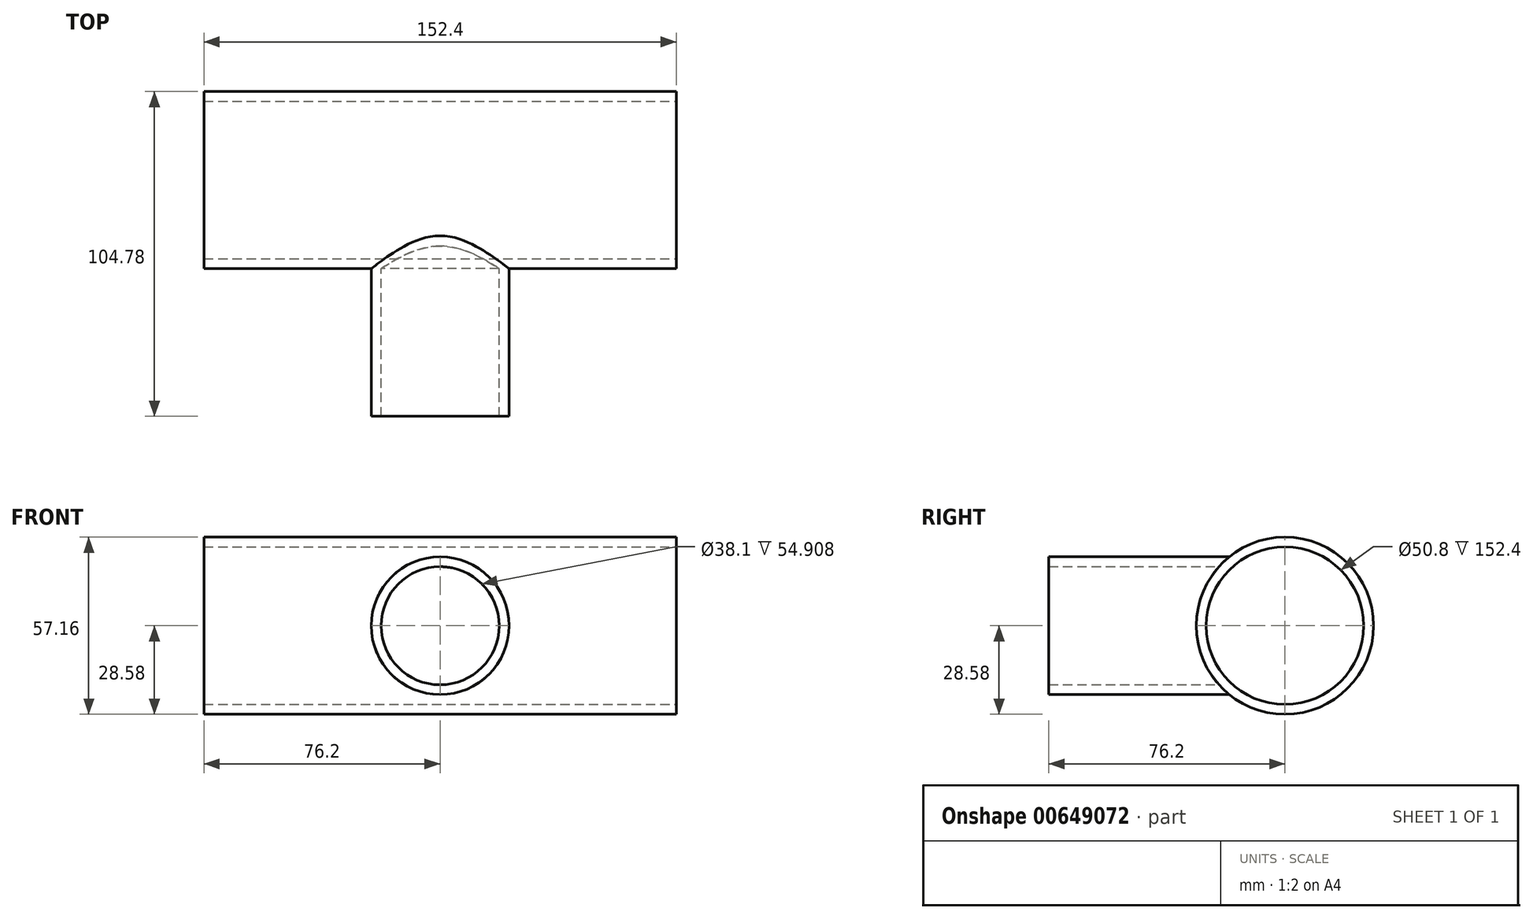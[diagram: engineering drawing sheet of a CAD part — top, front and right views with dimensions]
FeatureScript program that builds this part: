
annotation { "Feature Type Name" : "Feature", "Feature Type Description" : "" }
export const myFeature = defineFeature(function(context is Context, id is Id, definition is map)
    precondition{}
    {
        {
            var Q0;
            Q0=qCreatedBy(makeId("Right.planeOp"),FACE);
            var sketch = newSketch(context, id + "F0", { "sketchPlane" : qUnion([Q0])});
            skCircle(sketch, "E0", {"center": v(0, 0) * mm, "radius": 28.58 * mm});
            skSolve(sketch);
        }
        {
            var Q0;
            Q0 = qSketchRegion(id + "F0", true);
            extrude(context, id + "F1", {"entities" : qUnion([Q0]), "depth" : 76.2 * mm, "offsetDistance" : 25.4 * mm, "hasSecondDirection" : true, "secondDirectionOppositeDirection" : true, "secondDirectionDepth" : 76.2 * mm});
        }
        {
            var Q0;
            Q0=qCreatedBy(makeId("Front.planeOp"),FACE);
            var sketch = newSketch(context, id + "F2", { "sketchPlane" : qUnion([Q0])});
            skCircle(sketch, "E1", {"center": v(0, 0) * mm, "radius": 22.23 * mm});
            skCircle(sketch, "E2", {"center": v(0, 0) * mm, "radius": 19.05 * mm});
            skSolve(sketch);
        }
        {
            var Q0;
            Q0 = qSketchRegion(id + "F2", true);
            extrude(context, id + "F3", {"entities" : qUnion([Q0]), "operationType" : NewBodyOperationType.ADD, "depth" : 76.2 * mm, "offsetDistance" : 25.4 * mm});
        }
        {
            var Q0;
            Q0=makeQuery(id+"F1.opExtrude","CAP_FACE",FACE,{"disambiguationData":[OSD([sQuery(id+"F0.wireOp",EDGE,"E0")])],"isStart":false});
            var sketch = newSketch(context, id + "F4", { "sketchPlane" : qUnion([Q0])});
            skCircle(sketch, "E3", {"center": v(0, 0) * mm, "radius": 25.4 * mm});
            skSolve(sketch);
        }
        {
            var Q0;
            Q0 = qSketchRegion(id + "F4", true);
            extrude(context, id + "F5", {"entities" : qUnion([Q0]), "operationType" : NewBodyOperationType.REMOVE, "oppositeDirection" : true, "depth" : 152.4 * mm, "offsetDistance" : 25.4 * mm});
        }
    });
